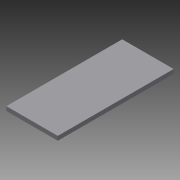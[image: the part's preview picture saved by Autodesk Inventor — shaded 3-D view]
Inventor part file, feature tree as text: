
AUTODESK INVENTOR PART (.ipt)
format: ipt  version: 2013 (Build 170138000, 138)  size: 66,048 bytes
history: native  units: mm
features: extrude x1, sketch x1
ambient origin geometry x8: Origin, YZ Plane, XZ Plane, XY Plane, X Axis, Y Axis, Z Axis, Center Point
bodies: Solid1 (feature_tree)
feature tree (2):
  extrude  "Extrusion1"  Depth=500.0mm
  sketch  "Sketch1"  dims[d0=222.0mm d1=500.0mm d2=18.0mm d3=0.0mm]
